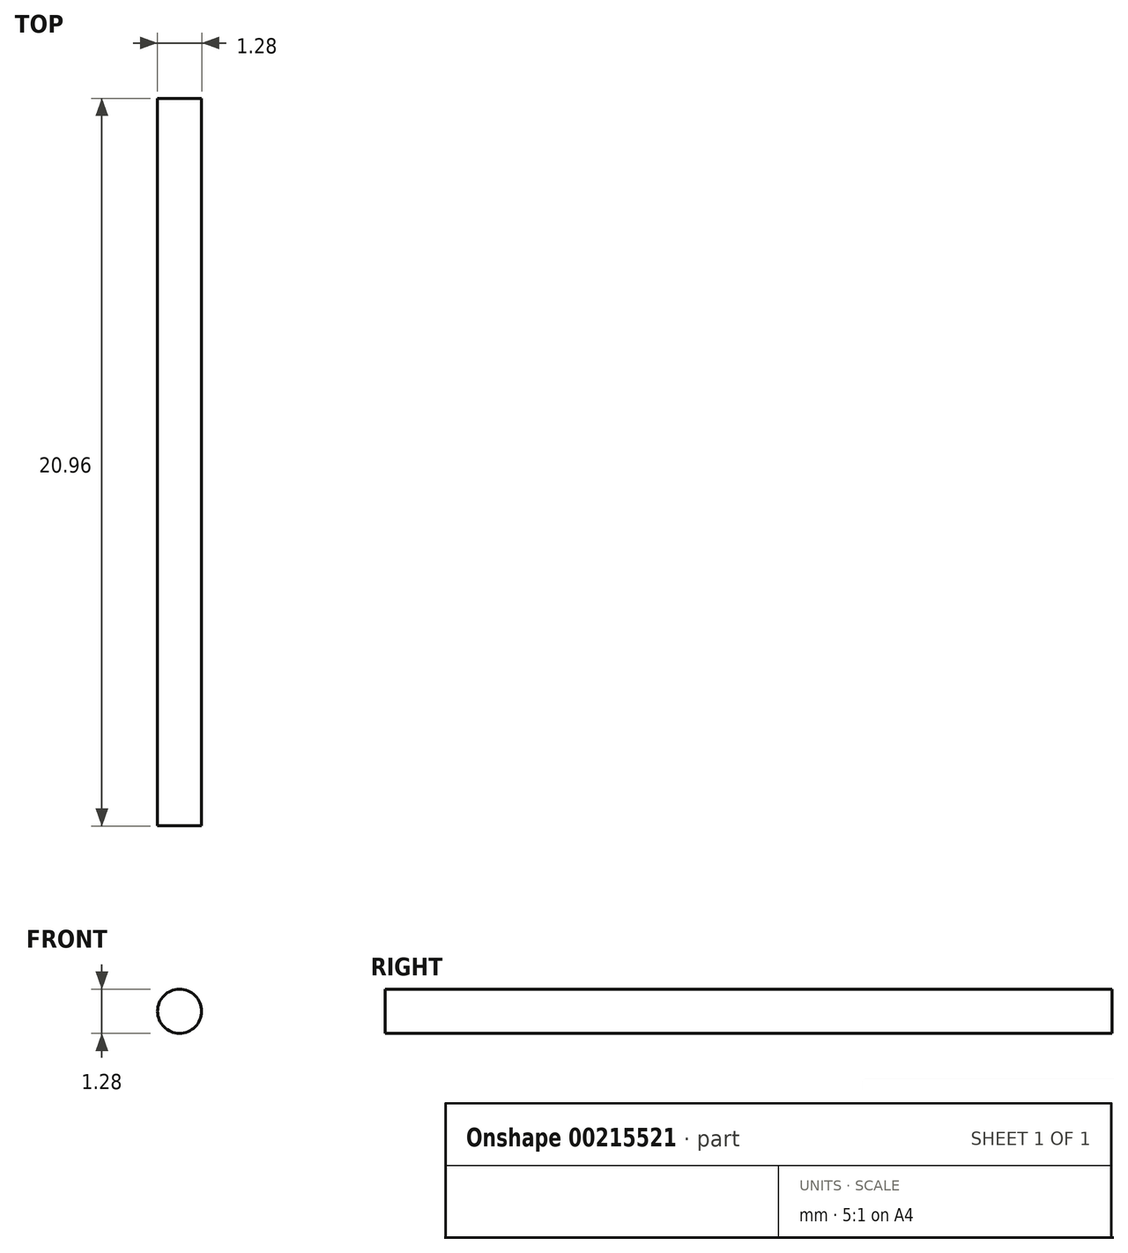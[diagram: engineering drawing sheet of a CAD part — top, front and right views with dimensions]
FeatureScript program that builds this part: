
annotation { "Feature Type Name" : "Feature", "Feature Type Description" : "" }
export const myFeature = defineFeature(function(context is Context, id is Id, definition is map)
    precondition{}
    {
        {
            var Q0;
            Q0=qCreatedBy(makeId("Front.planeOp"),FACE);
            var sketch = newSketch(context, id + "F0", { "sketchPlane" : qUnion([Q0])});
            skCircle(sketch, "E0", {"center": v(0, 0) * mm, "radius": 0.64 * mm});
            skSolve(sketch);
        }
        {
            var Q0;
            Q0 = qSketchRegion(id + "F0", true);
            extrude(context, id + "F1", {"entities" : qUnion([Q0]), "depth" : 20.95 * mm});
        }
    });
